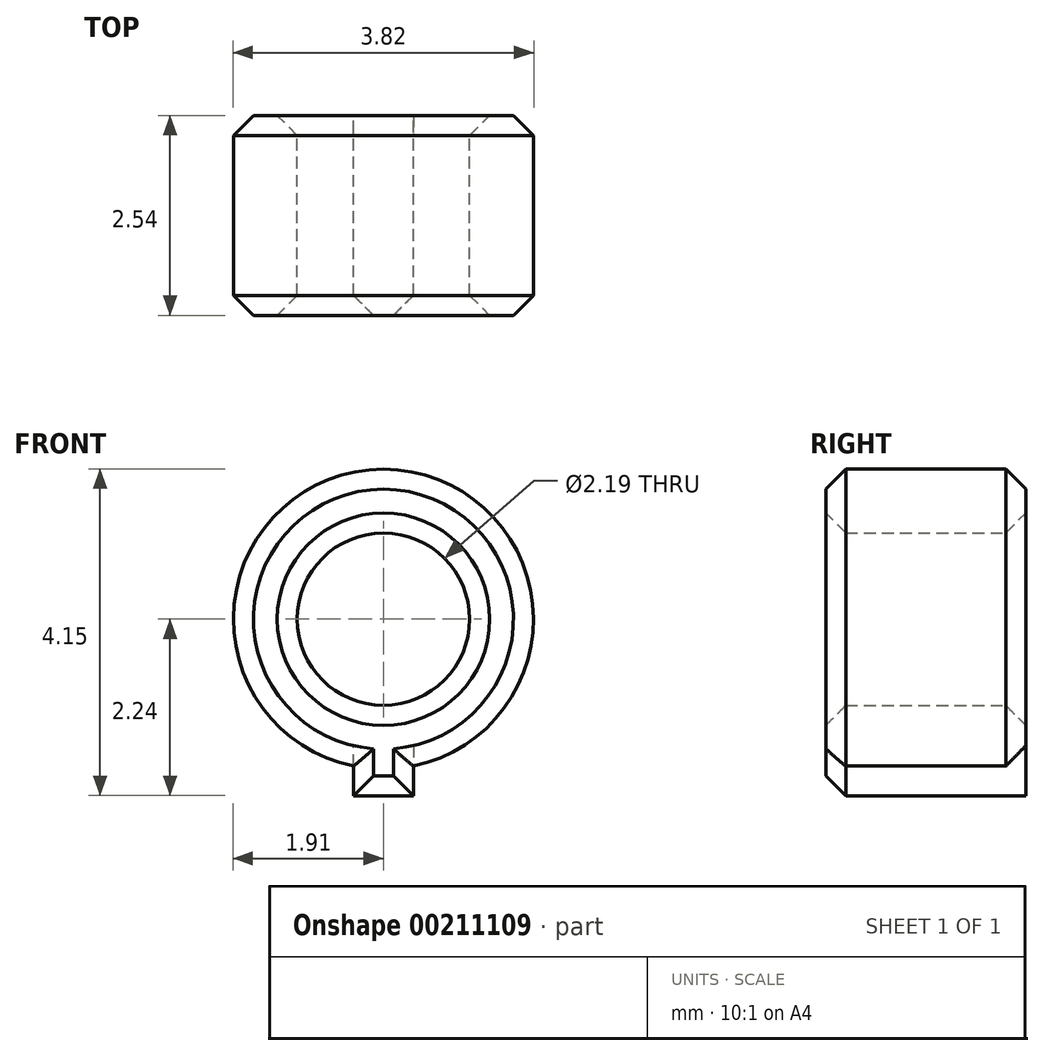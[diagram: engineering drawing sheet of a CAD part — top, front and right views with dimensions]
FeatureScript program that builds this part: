
annotation { "Feature Type Name" : "Feature", "Feature Type Description" : "" }
export const myFeature = defineFeature(function(context is Context, id is Id, definition is map)
    precondition{}
    {
        {
            var Q0;
            Q0=qCreatedBy(makeId("Front.planeOp"),FACE);
            var sketch = newSketch(context, id + "F1", { "sketchPlane" : qUnion([Q0])});
            skArc(sketch, "E0", {"start": v(0.38, -1.87) * mm, "mid": v(0, 1.9) * mm, "end": v(-0.38, -1.87) * mm});
            skCircle(sketch, "E1", {"center": v(0, 0) * mm, "radius": 1.1 * mm});
            skLineSegment(sketch, "E2.0", {"start": v(-0.38, -1.87) * mm, "end": v(-0.38, -2.24) * mm});
            skLineSegment(sketch, "E3.0", {"start": v(0.38, -1.87) * mm, "end": v(0.38, -2.24) * mm});
            skLineSegment(sketch, "E4", {"start": v(-0.38, -2.24) * mm, "end": v(0.38, -2.24) * mm});
            skPoint(sketch, "E5.orphan", {"position": v(0, -1.1) * mm});
            skSolve(sketch);
        }
        {
            var Q0;
            Q0=makeQuery(id+"F1.imprint","IMPRINT",FACE,{"disambiguationData":[TD([[makeQuery(id+"F1.imprint","IMPRINT",EDGE,{"derivedFrom":sQuery(id+"F1.wireOp",EDGE,"E0")}),1.0]])]});
            extrude(context, id + "F2", {"entities" : qUnion([Q0]), "depth" : 2.54 * mm});
        }
        {
            var Q0;
            Q0=makeQuery(id+"F2.opExtrude","CAP_EDGE",EDGE,{"disambiguationData":[OSD([sQuery(id+"F1.wireOp",EDGE,"E1")])],"isStart":false});
            var Q1;
            Q1=makeQuery(id+"F2.opExtrude","CAP_EDGE",EDGE,{"disambiguationData":[OSD([sQuery(id+"F1.wireOp",EDGE,"E1")])],"isStart":true});
            var Q2;
            Q2=makeQuery(id+"F2.opExtrude","CAP_EDGE",EDGE,{"disambiguationData":[OSD([sQuery(id+"F1.wireOp",EDGE,"E0")])],"isStart":true});
            var Q3;
            Q3=makeQuery(id+"F2.opExtrude","CAP_FACE",FACE,{"disambiguationData":[OSD([sQuery(id+"F1.wireOp",EDGE,"E0"),sQuery(id+"F1.wireOp",EDGE,"E1"),sQuery(id+"F1.wireOp",EDGE,"E2.0"),sQuery(id+"F1.wireOp",EDGE,"E3.0"),sQuery(id+"F1.wireOp",EDGE,"E4")])],"isStart":false});
            chamfer(context, id + "F0", {"entities" : qUnion([Q0, Q1, Q2, Q3]), "width" : 0.25 * mm, "tangentPropagation" : true});
        }
    });
